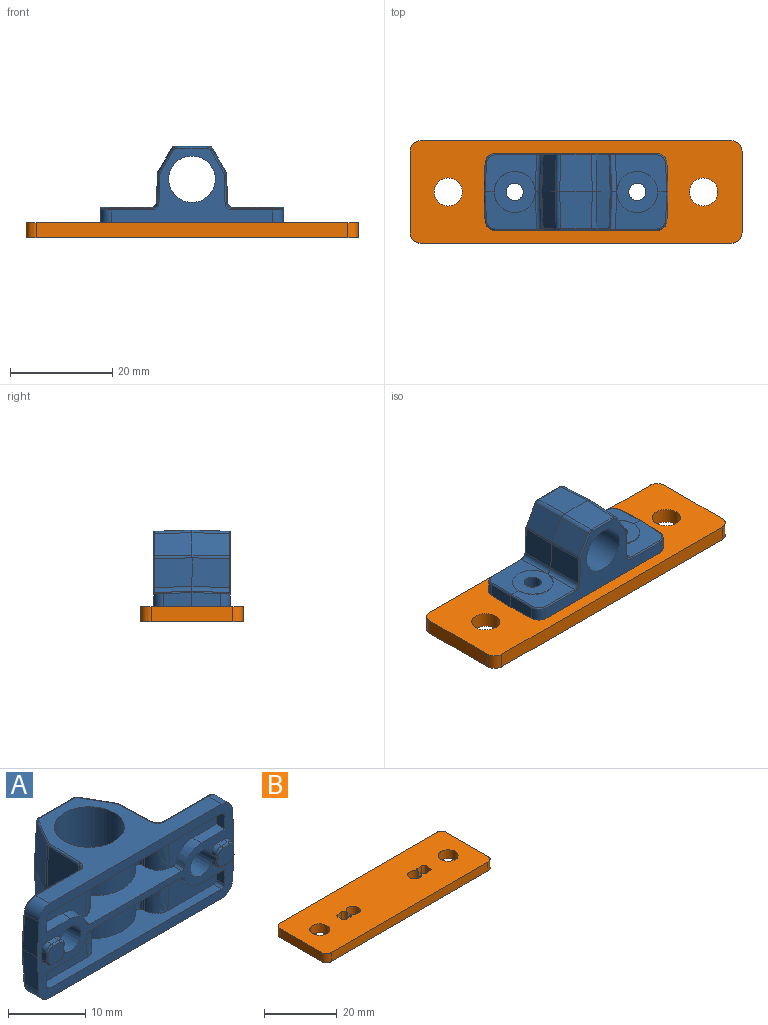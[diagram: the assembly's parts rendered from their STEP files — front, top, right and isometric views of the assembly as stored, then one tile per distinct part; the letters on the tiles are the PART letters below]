
ASSEMBLY  parts=2 mates=1
PART A: 158 faces, bbox 37.1x17.1x16.1 mm
  f0: cylinder r=4.55mm len=15mm, axis (0,0,1), area 428.8mm2, adj f5,f6
  f1: cone r=2.02mm half-angle=5deg, axis (0,-1,0), area 35.1mm2, adj f21,f52,f53,f106,f107
  f2: cone r=2.02mm half-angle=5deg, axis (0,-1,0), area 35.1mm2, adj f21,f70,f76,f138,f139
  f3: cylinder r=4mm len=8mm, axis (0,1,0), area 0.9mm2, adj f86,f106
  f4: cylinder r=4mm len=8mm, axis (0,1,0), area 0.9mm2, adj f89,f138
  f5: plane 31.63x14.51mm, normal (0,0,-1), area 152.8mm2, adj f0,f7,f8,f9,f10,f11,f12,f13
  f6: plane 31.62x14.5mm, normal (0,0,1), area 153mm2, adj f0,f21,f23,f24,f25,f26,f27,f28
  f7: cylinder r=0.25mm len=8.09mm, axis (1,0,0), area 3.1mm2, adj f5,f8,f38,f80
  f8: bspline ~1.25x1.22mm, area 0.6mm2, adj f5,f7,f9,f92
  f9: cylinder r=0.25mm len=5.76mm, axis (0.03,1,0), area 2.2mm2, adj f5,f8,f10,f39
  f10: bspline ~0.47x0.35mm, area 0.2mm2, adj f5,f9,f11,f93
  f11: cylinder r=0.25mm len=4.44mm, axis (0.5,0.87,0), area 1.9mm2, adj f5,f10,f12,f40
  f12: bspline ~0.87x0.62mm, area 0.4mm2, adj f5,f11,f13,f94
  f13: cylinder r=0.25mm len=6.06mm, axis (1,0,0), area 2.3mm2, adj f5,f12,f14,f41
  f14: bspline ~0.87x0.62mm, area 0.4mm2, adj f5,f13,f15,f95
  f15: cylinder r=0.25mm len=4.44mm, axis (0.5,-0.87,0), area 1.9mm2, adj f5,f14,f16,f42
  f16: bspline ~0.47x0.35mm, area 0.2mm2, adj f5,f15,f17,f96
  f17: cylinder r=0.25mm len=5.76mm, axis (0.03,-1,0), area 2.2mm2, adj f5,f16,f18,f43
  f18: bspline ~1.25x1.22mm, area 0.6mm2, adj f5,f17,f19,f97
  f19: cylinder r=0.25mm len=8.09mm, axis (1,0,0), area 3.1mm2, adj f5,f18,f44,f46
  f20: cylinder r=2mm len=2.56mm, axis (0,-1,0), area 7.8mm2, adj f5,f21,f45,f46
  f21: plane 36.11x15.11mm, normal (0,-1,0), area 201.1mm2, adj f1,f2,f5,f6,f20,f22,f35,f36
  f22: cylinder r=2mm len=2.56mm, axis (0,1,0), area 7.8mm2, adj f5,f21,f78,f80
  f23: bspline ~1.25x1.22mm, area 0.6mm2, adj f6,f24,f37,f143
  f24: cylinder r=0.25mm len=5.76mm, axis (-0.03,-1,0), area 2.2mm2, adj f6,f23,f25,f81
  f25: bspline ~0.47x0.35mm, area 0.2mm2, adj f6,f24,f26,f142
  f26: cylinder r=0.25mm len=4.44mm, axis (-0.5,-0.87,0), area 1.9mm2, adj f6,f25,f27,f82
  f27: bspline ~0.87x0.62mm, area 0.4mm2, adj f6,f26,f28,f144
  f28: cylinder r=0.25mm len=6.06mm, axis (-1,0,0), area 2.3mm2, adj f6,f27,f29,f83
  f29: bspline ~0.87x0.62mm, area 0.4mm2, adj f6,f28,f30,f145
  f30: cylinder r=0.25mm len=4.44mm, axis (-0.5,0.87,0), area 1.9mm2, adj f6,f29,f31,f84
  f31: bspline ~0.47x0.35mm, area 0.2mm2, adj f6,f30,f32,f146
  f32: cylinder r=0.25mm len=5.76mm, axis (-0.03,1,0), area 2.2mm2, adj f6,f31,f33,f85
  f33: bspline ~1.25x1.22mm, area 0.6mm2, adj f6,f32,f34,f147
  f34: cylinder r=0.25mm len=8.09mm, axis (-1,0,0), area 3.1mm2, adj f6,f33,f86,f87
  f35: cylinder r=2mm len=2.56mm, axis (0,1,0), area 7.8mm2, adj f6,f21,f77,f87
  f36: cylinder r=2mm len=2.56mm, axis (0,-1,0), area 7.8mm2, adj f6,f21,f79,f88
  f37: cylinder r=0.25mm len=8.09mm, axis (-1,0,0), area 3.1mm2, adj f6,f23,f88,f89
  f38: plane 11.17x8.4mm, normal (0,1,-0.03), area 45.3mm2, adj f7,f80,f89,f90,f91,f92
  f39: plane 7.26x5.83mm, normal (-1,0.03,-0.03), area 41.2mm2, adj f9,f81,f92,f93
  f40: plane 7.26x4.57mm, normal (-0.87,0.5,-0.03), area 37mm2, adj f11,f82,f93,f94
  f41: plane 7.26x6.35mm, normal (0,1,-0.03), area 45.1mm2, adj f13,f83,f94,f95
  f42: plane 7.26x4.57mm, normal (0.87,0.5,-0.03), area 37mm2, adj f15,f84,f95,f96
  f43: plane 7.26x5.83mm, normal (1,0.03,-0.03), area 41.2mm2, adj f17,f85,f96,f97
  f44: plane 11.17x8.4mm, normal (0,1,-0.03), area 45.3mm2, adj f19,f46,f86,f97,f98,f99
  f45: plane 5.57x2.75mm, normal (1,0,-0.03), area 14.8mm2, adj f20,f21,f77,f99
  f46: bspline ~2x1.93mm, area 1.1mm2, adj f19,f20,f44,f99
  f47: plane 1.39x0.77mm, normal (0,-0.09,-1), area 1mm2, adj f21,f48,f53,f100
  f48: cylinder r=1mm len=1.06mm, axis (-0.09,-0.99,0.09), area 1.2mm2, adj f21,f47,f49,f101
  f49: plane 1.38x0.77mm, normal (1,-0.09,0), area 1mm2, adj f21,f48,f50,f102
  f50: cylinder r=1mm len=1.06mm, axis (-0.09,-0.99,-0.09), area 1.2mm2, adj f21,f49,f51,f103
  f51: plane 1.39x0.77mm, normal (0,-0.09,1), area 1mm2, adj f21,f50,f52,f104
  f52: bspline ~1.27x1.08mm, area 1.4mm2, adj f1,f21,f51,f105
  f53: bspline ~1.27x1.12mm, area 1.4mm2, adj f1,f21,f47,f108
  f54: plane 17.28x5.06mm, normal (0,-0.09,-1), area 47.9mm2, adj f21,f109,f110,f111,f112,f113,f114,f116
  f55: cone r=3.32mm half-angle=5deg, axis (0,1,0), area 6.3mm2, adj f21,f56,f112,f114
  f56: plane 4.39x1.5mm, normal (0,-0.09,-1), area 6.6mm2, adj f21,f55,f57,f114
  f57: plane 2.33x1.5mm, normal (1,0,0.03), area 3.4mm2, adj f21,f56,f114,f115
  f58: plane 31.64x4.53mm, normal (0,0,1), area 68mm2, adj f21,f109,f110,f111,f114,f115,f116,f117
  f59: plane 2.33x1.5mm, normal (-1,0,0.03), area 3.4mm2, adj f21,f60,f117,f118
  f60: plane 4.39x1.5mm, normal (0,-0.09,-1), area 6.6mm2, adj f21,f59,f61,f118
  f61: cone r=3.32mm half-angle=5deg, axis (0,1,0), area 6.3mm2, adj f21,f60,f113,f118
  f62: cone r=3.32mm half-angle=5deg, axis (0,1,0), area 6.3mm2, adj f21,f63,f120,f121
  f63: plane 4.39x1.5mm, normal (0,-0.09,1), area 6.6mm2, adj f21,f62,f64,f120
  f64: plane 2.33x1.5mm, normal (-1,0,-0.03), area 3.4mm2, adj f21,f63,f120,f122
  f65: plane 31.64x4.53mm, normal (0,0,-1), area 68mm2, adj f21,f120,f122,f123,f124,f125,f126,f127
  f66: plane 2.33x1.5mm, normal (1,0,-0.03), area 3.4mm2, adj f21,f67,f125,f126
  f67: plane 4.39x1.5mm, normal (0,-0.09,1), area 6.6mm2, adj f21,f66,f68,f126
  f68: cone r=3.32mm half-angle=5deg, axis (0,1,0), area 6.3mm2, adj f21,f67,f126,f128
  f69: plane 17.28x5.06mm, normal (0,-0.09,1), area 47.8mm2, adj f21,f120,f121,f123,f124,f126,f127,f128
  f70: bspline ~1.27x1.12mm, area 1.4mm2, adj f2,f21,f71,f131
  f71: plane 1.39x0.77mm, normal (0,-0.09,1), area 1mm2, adj f21,f70,f72,f132
  f72: cylinder r=1mm len=1.06mm, axis (0.09,-0.99,-0.09), area 1.2mm2, adj f21,f71,f73,f133
  f73: plane 1.38x0.77mm, normal (-1,-0.09,0), area 1mm2, adj f21,f72,f74,f134
  f74: cylinder r=1mm len=1.06mm, axis (0.09,-0.99,0.09), area 1.2mm2, adj f21,f73,f75,f135
  f75: plane 1.39x0.77mm, normal (0,-0.09,-1), area 1mm2, adj f21,f74,f76,f136
  f76: bspline ~1.27x1.08mm, area 1.4mm2, adj f2,f21,f75,f137
  f77: plane 5.57x2.75mm, normal (1,0,0.03), area 14.8mm2, adj f21,f35,f45,f140
  f78: plane 5.57x2.75mm, normal (-1,0,-0.03), area 14.8mm2, adj f21,f22,f79,f91
  f79: plane 5.57x2.75mm, normal (-1,0,0.03), area 14.8mm2, adj f21,f36,f78,f141
  f80: bspline ~2x1.93mm, area 1.1mm2, adj f7,f22,f38,f91
  f81: plane 7.26x5.83mm, normal (-1,0.03,0.03), area 41.2mm2, adj f24,f39,f142,f143
  f82: plane 7.26x4.57mm, normal (-0.87,0.5,0.03), area 37mm2, adj f26,f40,f142,f144
  f83: plane 7.26x6.35mm, normal (0,1,0.03), area 45.1mm2, adj f28,f41,f144,f145
  f84: plane 7.26x4.57mm, normal (0.87,0.5,0.03), area 37mm2, adj f30,f42,f145,f146
  f85: plane 7.26x5.83mm, normal (1,0.03,0.03), area 41.2mm2, adj f32,f43,f146,f147
  f86: plane 10.17x7.4mm, normal (0,1,0.03), area 45.3mm2, adj f3,f34,f44,f87,f140,f147
  f87: bspline ~2x1.93mm, area 1.1mm2, adj f34,f35,f86,f140
  f88: bspline ~2x1.93mm, area 1.1mm2, adj f36,f37,f89,f141
  f89: plane 10.17x7.4mm, normal (0,1,0.03), area 45.3mm2, adj f4,f37,f38,f88,f141,f143
  f90: cylinder r=4mm len=8mm, axis (0,1,0), area 0mm2, adj f38,f138
  f91: cylinder r=0.25mm len=5.57mm, axis (-0.03,0.03,1), area 2.2mm2, adj f38,f78,f80,f141
  f92: cylinder r=1mm len=7.27mm, axis (0.03,-0.03,-1), area 11.2mm2, adj f8,f38,f39,f143
  f93: cylinder r=1mm len=7.26mm, axis (0.03,-0.01,-1), area 3.5mm2, adj f10,f39,f40,f142
  f94: cylinder r=1mm len=7.26mm, axis (0.02,-0.03,-1), area 7.6mm2, adj f12,f40,f41,f144
  f95: cylinder r=1mm len=7.26mm, axis (-0.02,-0.03,-1), area 7.6mm2, adj f14,f41,f42,f145
  f96: cylinder r=1mm len=7.26mm, axis (-0.03,-0.01,-1), area 3.5mm2, adj f16,f42,f43,f146
  f97: cylinder r=1mm len=7.27mm, axis (-0.03,-0.03,-1), area 11.2mm2, adj f18,f43,f44,f147
  f98: cylinder r=4mm len=8mm, axis (0,1,0), area 0mm2, adj f44,f106
  f99: cylinder r=0.25mm len=5.57mm, axis (-0.03,-0.03,-1), area 2.2mm2, adj f44,f45,f46,f140
  f100: cylinder r=0.25mm len=1.24mm, axis (-1,0,0), area 0.5mm2, adj f47,f101,f108,f148
  f101: bspline ~1x1mm, area 0.5mm2, adj f48,f100,f102,f148
  f102: cylinder r=0.25mm len=1.24mm, axis (0,0,-1), area 0.5mm2, adj f49,f101,f103,f148
  f103: bspline ~1x1mm, area 0.5mm2, adj f50,f102,f104,f148
  f104: cylinder r=0.25mm len=1.24mm, axis (1,0,0), area 0.5mm2, adj f51,f103,f105,f148
  f105: bspline ~1.2x1.01mm, area 0.6mm2, adj f52,f104,f107,f148
  f106: plane 8x8mm, normal (0,1,0), area 41.3mm2, adj f1,f3,f98
  f107: torus R=2.26mm, axis (0,-1,0), area 0.3mm2, adj f1,f105,f108,f148
  f108: bspline ~1.2x1.01mm, area 0.6mm2, adj f53,f100,f107,f148
  f109: cylinder r=2.5mm len=5.4mm, axis (-0.03,-0.03,-1), area 11.8mm2, adj f54,f58,f119,f149
  f110: cylinder r=6.05mm len=9.1mm, axis (0,0,1), area 51.4mm2, adj f54,f58,f150,f151
  f111: cylinder r=2.5mm len=5.4mm, axis (0.03,-0.03,-1), area 11.8mm2, adj f54,f58,f116,f152
  f112: bspline ~1.53x0.58mm, area 1mm2, adj f21,f54,f55,f114
  f113: bspline ~1.53x0.58mm, area 1mm2, adj f21,f54,f61,f118
  f114: plane 9.05x5.39mm, normal (0,-1,0), area 28.9mm2, adj f54,f55,f56,f57,f58,f112,f115,f116
  f115: cylinder r=0.5mm len=1.5mm, axis (0,1,0), area 1.2mm2, adj f21,f57,f58,f114
  f116: bspline ~5.55x2.09mm, area 7.4mm2, adj f54,f58,f111,f114
  f117: cylinder r=0.5mm len=1.5mm, axis (0,1,0), area 1.2mm2, adj f21,f58,f59,f118
  f118: plane 9.05x5.39mm, normal (0,-1,0), area 28.9mm2, adj f54,f58,f59,f60,f61,f113,f117,f119
  f119: bspline ~5.55x2.09mm, area 7.4mm2, adj f54,f58,f109,f118
  f120: plane 9.05x5.39mm, normal (0,-1,0), area 28.9mm2, adj f62,f63,f64,f65,f69,f121,f122,f124
  f121: bspline ~1.53x0.58mm, area 1mm2, adj f21,f62,f69,f120
  f122: cylinder r=0.5mm len=1.5mm, axis (0,1,0), area 1.2mm2, adj f21,f64,f65,f120
  f123: cylinder r=6.05mm len=9.1mm, axis (0,0,1), area 51.4mm2, adj f65,f69,f153,f154
  f124: bspline ~5.55x2.09mm, area 7.4mm2, adj f65,f69,f120,f130
  f125: cylinder r=0.5mm len=1.5mm, axis (0,1,0), area 1.2mm2, adj f21,f65,f66,f126
  f126: plane 9.05x5.39mm, normal (0,-1,0), area 28.9mm2, adj f65,f66,f67,f68,f69,f125,f127,f128
  f127: bspline ~5.55x2.09mm, area 7.4mm2, adj f65,f69,f126,f129
  f128: bspline ~1.53x0.58mm, area 1mm2, adj f21,f68,f69,f126
  f129: cylinder r=2.5mm len=5.4mm, axis (-0.03,0.03,-1), area 11.8mm2, adj f65,f69,f127,f155
  f130: cylinder r=2.5mm len=5.4mm, axis (0.03,0.03,-1), area 11.8mm2, adj f65,f69,f124,f156
  f131: bspline ~1.2x1.01mm, area 0.6mm2, adj f70,f132,f139,f157
  f132: cylinder r=0.25mm len=1.24mm, axis (-1,0,0), area 0.5mm2, adj f71,f131,f133,f157
  f133: bspline ~1x1mm, area 0.5mm2, adj f72,f132,f134,f157
  f134: cylinder r=0.25mm len=1.24mm, axis (0,0,-1), area 0.5mm2, adj f73,f133,f135,f157
  f135: bspline ~1x1mm, area 0.5mm2, adj f74,f134,f136,f157
  f136: cylinder r=0.25mm len=1.24mm, axis (1,0,0), area 0.5mm2, adj f75,f135,f137,f157
  f137: bspline ~1.2x1.01mm, area 0.6mm2, adj f76,f136,f139,f157
  f138: plane 8x8mm, normal (0,1,0), area 41.3mm2, adj f2,f4,f90
  f139: torus R=2.26mm, axis (0,1,0), area 0.3mm2, adj f2,f131,f137,f157
  f140: cylinder r=0.25mm len=5.57mm, axis (0.03,0.03,-1), area 2.2mm2, adj f77,f86,f87,f99
  f141: cylinder r=0.25mm len=5.57mm, axis (0.03,-0.03,1), area 2.2mm2, adj f79,f88,f89,f91
  f142: cylinder r=1mm len=7.26mm, axis (-0.03,0.01,-1), area 3.5mm2, adj f25,f81,f82,f93
  f143: cylinder r=1mm len=7.27mm, axis (-0.03,0.03,-1), area 11.2mm2, adj f23,f81,f89,f92
  f144: cylinder r=1mm len=7.26mm, axis (-0.02,0.03,-1), area 7.6mm2, adj f27,f82,f83,f94
  f145: cylinder r=1mm len=7.26mm, axis (0.02,0.03,-1), area 7.6mm2, adj f29,f83,f84,f95
  f146: cylinder r=1mm len=7.26mm, axis (0.03,0.01,-1), area 3.5mm2, adj f31,f84,f85,f96
  f147: cylinder r=1mm len=7.27mm, axis (0.03,0.03,-1), area 11.2mm2, adj f33,f85,f86,f97
  f148: plane 2.76x2.76mm, normal (0,-1,0), area 7mm2, adj f100,f101,f102,f103,f104,f105,f107,f108
  f149: plane 5.16x0.5mm, normal (-1,-0.03,0.03), area 1.6mm2, adj f54,f58,f109,f150
  f150: bspline ~5.18x1.04mm, area 6.1mm2, adj f54,f58,f110,f149
  f151: bspline ~5.18x1.04mm, area 6.1mm2, adj f54,f58,f110,f152
  f152: plane 5.16x0.5mm, normal (1,-0.03,0.03), area 1.6mm2, adj f54,f58,f111,f151
  f153: bspline ~5.18x1.04mm, area 6.1mm2, adj f65,f69,f123,f155
  f154: bspline ~5.18x1.04mm, area 6.1mm2, adj f65,f69,f123,f156
  f155: plane 5.16x0.5mm, normal (1,-0.03,-0.03), area 1.6mm2, adj f65,f69,f129,f153
  f156: plane 5.16x0.5mm, normal (-1,-0.03,-0.03), area 1.6mm2, adj f65,f69,f130,f154
  f157: plane 2.76x2.76mm, normal (0,-1,0), area 7mm2, adj f131,f132,f133,f134,f135,f136,f137,f139
PART B: 32 faces, bbox 65x20x3 mm
  f0: plane 16x3mm, normal (-1,0,0), area 48mm2, adj f1,f29,f30,f31
  f1: cylinder r=2mm len=3mm, axis (0,0,-1), area 9.4mm2, adj f0,f2,f30,f31
  f2: plane 61x3mm, normal (0,-1,0), area 183mm2, adj f1,f3,f30,f31
  f3: cylinder r=2mm len=3mm, axis (0,0,-1), area 9.4mm2, adj f2,f4,f30,f31
  f4: plane 16x3mm, normal (1,0,0), area 48mm2, adj f3,f5,f30,f31
  f5: cylinder r=2mm len=3mm, axis (0,0,-1), area 9.4mm2, adj f4,f6,f30,f31
  f6: plane 61x3mm, normal (0,1,0), area 183mm2, adj f5,f29,f30,f31
  f7: plane 3x0.15mm, normal (1,0,0), area 0.5mm2, adj f8,f25,f30,f31
  f8: cylinder r=1.95mm len=3.9mm, axis (0,0,-1), area 33.5mm2, adj f7,f9,f30,f31
  f9: plane 3x0.15mm, normal (1,0,0), area 0.5mm2, adj f8,f10,f30,f31
  f10: cylinder r=1mm len=3mm, axis (0,0,-1), area 4.7mm2, adj f9,f11,f30,f31
  f11: plane 3x1.38mm, normal (0,-1,0), area 4.1mm2, adj f10,f12,f30,f31
  f12: cylinder r=1mm len=3mm, axis (0,0,-1), area 4.7mm2, adj f11,f13,f30,f31
  f13: plane 3x1.38mm, normal (-1,0,0), area 4.1mm2, adj f12,f14,f30,f31
  f14: cylinder r=1mm len=3mm, axis (0,0,-1), area 4.7mm2, adj f13,f15,f30,f31
  f15: plane 3x1.38mm, normal (0,1,0), area 4.1mm2, adj f14,f25,f30,f31
  f16: cylinder r=1.95mm len=3.9mm, axis (0,0,-1), area 33.5mm2, adj f17,f28,f30,f31
  f17: plane 3x0.15mm, normal (-1,0,0), area 0.5mm2, adj f16,f18,f30,f31
  f18: cylinder r=1mm len=3mm, axis (0,0,-1), area 4.7mm2, adj f17,f19,f30,f31
  f19: plane 3x1.38mm, normal (0,1,0), area 4.1mm2, adj f18,f20,f30,f31
  f20: cylinder r=1mm len=3mm, axis (0,0,-1), area 4.7mm2, adj f19,f21,f30,f31
  f21: plane 3x1.38mm, normal (1,0,0), area 4.1mm2, adj f20,f22,f30,f31
  f22: cylinder r=1mm len=3mm, axis (0,0,-1), area 4.7mm2, adj f21,f23,f30,f31
  f23: plane 3x1.38mm, normal (0,-1,0), area 4.1mm2, adj f22,f24,f30,f31
  f24: cylinder r=1mm len=3mm, axis (0,0,-1), area 4.7mm2, adj f23,f28,f30,f31
  f25: cylinder r=1mm len=3mm, axis (0,0,-1), area 4.7mm2, adj f7,f15,f30,f31
  f26: cylinder r=2.75mm len=5.5mm, axis (0,0,-1), area 51.8mm2, adj f30,f31
  f27: cylinder r=2.75mm len=5.5mm, axis (0,0,-1), area 51.8mm2, adj f30,f31
  f28: plane 3x0.15mm, normal (-1,0,0), area 0.5mm2, adj f16,f24,f30,f31
  f29: cylinder r=2mm len=3mm, axis (0,0,-1), area 9.4mm2, adj f0,f6,f30,f31
  f30: plane 65x20mm, normal (0,0,1), area 1204.2mm2, adj f0,f1,f2,f3,f4,f5,f6,f7
  f31: plane 65x20mm, normal (0,0,-1), area 1204.2mm2, adj f0,f1,f2,f3,f4,f5,f6,f7
PLACE A rot(axis=(1,0,0),90deg) t=(0,0,11.5)mm
PLACE B at identity fixed
MATE fastened A.f2 <-> B.f16  axis (0,0,1) through (-12,0,3)mm
